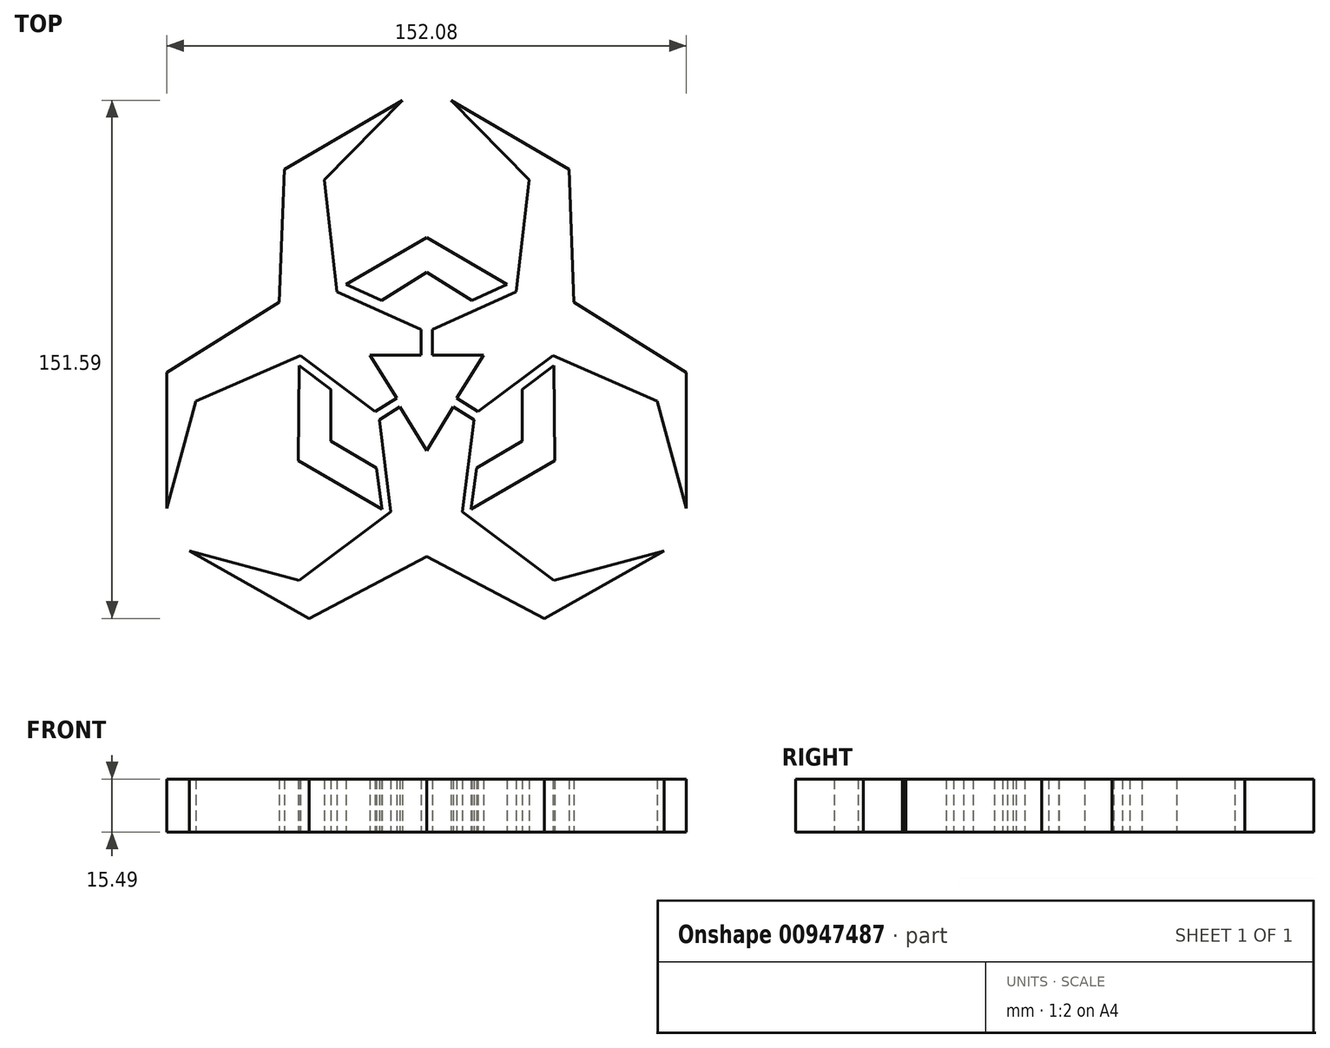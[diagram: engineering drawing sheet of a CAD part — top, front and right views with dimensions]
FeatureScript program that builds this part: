
annotation { "Feature Type Name" : "Feature", "Feature Type Description" : "" }
export const myFeature = defineFeature(function(context is Context, id is Id, definition is map)
    precondition{}
    {
        {
            var Q0;
            Q0=qCreatedBy(makeId("Top.planeOp"),FACE);
            var sketch = newSketch(context, id + "F0", { "sketchPlane" : qUnion([Q0])});
            skLineSegment(sketch, "E0", {"start": v(-13.19, 17.58) * mm, "end": v(-23.54, 22.27) * mm});
            skLineSegment(sketch, "E1", {"start": v(-23.54, 22.27) * mm, "end": v(0, 35.95) * mm});
            skLineSegment(sketch, "E2", {"start": v(0, 35.95) * mm, "end": v(0, 25.8) * mm});
            skLineSegment(sketch, "E3", {"start": v(0, 25.8) * mm, "end": v(-13.19, 17.58) * mm});
            skLineSegment(sketch, "E4.MirrorCS", {"start": v(23.54, 22.27) * mm, "end": v(0, 35.95) * mm});
            skLineSegment(sketch, "E5.MirrorCS", {"start": v(0, 25.8) * mm, "end": v(13.19, 17.58) * mm});
            skLineSegment(sketch, "E6.MirrorCS", {"start": v(13.19, 17.58) * mm, "end": v(23.54, 22.27) * mm});
            skLineSegment(sketch, "E7", {"start": v(-7.1, 76.07) * mm, "end": v(-41.67, 55.83) * mm});
            skLineSegment(sketch, "E8", {"start": v(-41.67, 55.83) * mm, "end": v(-43.14, 17.08) * mm});
            skLineSegment(sketch, "E9", {"start": v(-43.14, 17.08) * mm, "end": v(-76.04, -3.52) * mm});
            skLineSegment(sketch, "E10", {"start": v(-76.04, -3.52) * mm, "end": v(-76, -43.3) * mm});
            skLineSegment(sketch, "E11", {"start": v(-76, -43.3) * mm, "end": v(-67.53, -11.95) * mm});
            skLineSegment(sketch, "E12", {"start": v(-67.53, -11.95) * mm, "end": v(-36.97, 1.41) * mm});
            skLineSegment(sketch, "E13", {"start": v(-36.97, 1.41) * mm, "end": v(-15.01, -14.97) * mm});
            skLineSegment(sketch, "E14", {"start": v(-15.01, -14.97) * mm, "end": v(-8.76, -11.05) * mm});
            skLineSegment(sketch, "E15", {"start": v(-8.76, -11.05) * mm, "end": v(-16.63, 1.52) * mm});
            skLineSegment(sketch, "E16", {"start": v(-16.63, 1.52) * mm, "end": v(-1.65, 1.53) * mm});
            skLineSegment(sketch, "E17", {"start": v(-1.65, 1.53) * mm, "end": v(-1.66, 9.08) * mm});
            skLineSegment(sketch, "E18", {"start": v(-1.66, 9.08) * mm, "end": v(-26.24, 20.12) * mm});
            skLineSegment(sketch, "E19", {"start": v(-26.24, 20.12) * mm, "end": v(-29.96, 52.9) * mm});
            skLineSegment(sketch, "E20", {"start": v(-29.96, 52.9) * mm, "end": v(-7.1, 76.07) * mm});
            skLineSegment(sketch, "E21", {"start": v(-37.27, -1.5) * mm, "end": v(-28, -8.54) * mm});
            skLineSegment(sketch, "E22", {"start": v(-28, -8.54) * mm, "end": v(-28, -23.58) * mm});
            skLineSegment(sketch, "E23", {"start": v(-28, -23.58) * mm, "end": v(-14.7, -31.5) * mm});
            skLineSegment(sketch, "E24", {"start": v(-14.7, -31.5) * mm, "end": v(-13.03, -43.5) * mm});
            skLineSegment(sketch, "E25", {"start": v(-13.03, -43.5) * mm, "end": v(-37.54, -29.34) * mm});
            skLineSegment(sketch, "E26", {"start": v(-37.54, -29.34) * mm, "end": v(-37.27, -1.5) * mm});
            skLineSegment(sketch, "E27", {"start": v(0, -26.47) * mm, "end": v(0, -57.34) * mm});
            skLineSegment(sketch, "E28", {"start": v(0, -57.34) * mm, "end": v(-34.42, -75.52) * mm});
            skLineSegment(sketch, "E29", {"start": v(-34.42, -75.52) * mm, "end": v(-69.48, -55.78) * mm});
            skLineSegment(sketch, "E30", {"start": v(-69.48, -55.78) * mm, "end": v(-37.27, -64.33) * mm});
            skLineSegment(sketch, "E31", {"start": v(-37.27, -64.33) * mm, "end": v(-10.5, -44.28) * mm});
            skLineSegment(sketch, "E32", {"start": v(-10.5, -44.28) * mm, "end": v(-13.84, -17.43) * mm});
            skLineSegment(sketch, "E33", {"start": v(-13.84, -17.43) * mm, "end": v(-7.8, -13.6) * mm});
            skLineSegment(sketch, "E34", {"start": v(-7.8, -13.6) * mm, "end": v(0, -26.47) * mm});
            skLineSegment(sketch, "E35.MirrorCS", {"start": v(29.96, 52.9) * mm, "end": v(7.1, 76.07) * mm});
            skLineSegment(sketch, "E36.MirrorCS", {"start": v(7.1, 76.07) * mm, "end": v(41.67, 55.83) * mm});
            skLineSegment(sketch, "E37.MirrorCS", {"start": v(41.67, 55.83) * mm, "end": v(43.14, 17.08) * mm});
            skLineSegment(sketch, "E38.MirrorCS", {"start": v(26.24, 20.12) * mm, "end": v(29.96, 52.9) * mm});
            skLineSegment(sketch, "E39.MirrorCS", {"start": v(1.66, 9.08) * mm, "end": v(26.24, 20.12) * mm});
            skLineSegment(sketch, "E40.MirrorCS", {"start": v(16.63, 1.52) * mm, "end": v(1.65, 1.53) * mm});
            skLineSegment(sketch, "E41.MirrorCS", {"start": v(1.65, 1.53) * mm, "end": v(1.66, 9.08) * mm});
            skLineSegment(sketch, "E42.MirrorCS", {"start": v(13.84, -17.43) * mm, "end": v(7.8, -13.6) * mm});
            skLineSegment(sketch, "E43.MirrorCS", {"start": v(7.8, -13.6) * mm, "end": v(0, -26.47) * mm});
            skLineSegment(sketch, "E44.MirrorCS", {"start": v(8.76, -11.05) * mm, "end": v(16.63, 1.52) * mm});
            skLineSegment(sketch, "E45.MirrorCS", {"start": v(15.01, -14.97) * mm, "end": v(8.76, -11.05) * mm});
            skLineSegment(sketch, "E46.MirrorCS", {"start": v(36.97, 1.41) * mm, "end": v(15.01, -14.97) * mm});
            skLineSegment(sketch, "E47.MirrorCS", {"start": v(28, -8.54) * mm, "end": v(28, -23.58) * mm});
            skLineSegment(sketch, "E48.MirrorCS", {"start": v(37.27, -1.5) * mm, "end": v(28, -8.54) * mm});
            skLineSegment(sketch, "E49.MirrorCS", {"start": v(37.54, -29.34) * mm, "end": v(37.27, -1.5) * mm});
            skLineSegment(sketch, "E50.MirrorCS", {"start": v(13.03, -43.5) * mm, "end": v(37.54, -29.34) * mm});
            skLineSegment(sketch, "E51.MirrorCS", {"start": v(28, -23.58) * mm, "end": v(14.7, -31.5) * mm});
            skLineSegment(sketch, "E52.MirrorCS", {"start": v(14.7, -31.5) * mm, "end": v(13.03, -43.5) * mm});
            skLineSegment(sketch, "E53.MirrorCS", {"start": v(37.27, -64.33) * mm, "end": v(10.5, -44.28) * mm});
            skLineSegment(sketch, "E54.MirrorCS", {"start": v(10.5, -44.28) * mm, "end": v(13.84, -17.43) * mm});
            skLineSegment(sketch, "E55.MirrorCS", {"start": v(0, -57.34) * mm, "end": v(34.42, -75.52) * mm});
            skLineSegment(sketch, "E56.MirrorCS", {"start": v(34.42, -75.52) * mm, "end": v(69.48, -55.78) * mm});
            skLineSegment(sketch, "E57.MirrorCS", {"start": v(69.48, -55.78) * mm, "end": v(37.27, -64.33) * mm});
            skLineSegment(sketch, "E58.MirrorCS", {"start": v(67.53, -11.95) * mm, "end": v(36.97, 1.41) * mm});
            skLineSegment(sketch, "E59.MirrorCS", {"start": v(76, -43.3) * mm, "end": v(67.53, -11.95) * mm});
            skLineSegment(sketch, "E60.MirrorCS", {"start": v(76.04, -3.52) * mm, "end": v(76, -43.3) * mm});
            skLineSegment(sketch, "E61.MirrorCS", {"start": v(43.14, 17.08) * mm, "end": v(76.04, -3.52) * mm});
            skSolve(sketch);
        }
        {
            var Q0;
            Q0=makeQuery(id+"F0.imprint","IMPRINT",FACE,{"disambiguationData":[TD([[makeQuery(id+"F0.imprint","IMPRINT",EDGE,{"derivedFrom":sQuery(id+"F0.wireOp",EDGE,"E7")}),1.0]])]});
            var Q1;
            Q1=makeQuery(id+"F0.imprint","IMPRINT",FACE,{"disambiguationData":[TD([[makeQuery(id+"F0.imprint","IMPRINT",EDGE,{"derivedFrom":sQuery(id+"F0.wireOp",EDGE,"E35.MirrorCS")}),-1.0]])]});
            var Q2;
            Q2=makeQuery(id+"F0.imprint","IMPRINT",FACE,{"disambiguationData":[TD([[makeQuery(id+"F0.imprint","IMPRINT",EDGE,{"derivedFrom":sQuery(id+"F0.wireOp",EDGE,"E0")}),-1.0]])]});
            var Q3;
            Q3=makeQuery(id+"F0.imprint","IMPRINT",FACE,{"disambiguationData":[TD([[makeQuery(id+"F0.imprint","IMPRINT",EDGE,{"derivedFrom":sQuery(id+"F0.wireOp",EDGE,"E2")}),1.0]])]});
            var Q4;
            Q4=makeQuery(id+"F0.imprint","IMPRINT",FACE,{"disambiguationData":[TD([[makeQuery(id+"F0.imprint","IMPRINT",EDGE,{"derivedFrom":sQuery(id+"F0.wireOp",EDGE,"E27")}),-1.0]])]});
            var Q5;
            Q5=makeQuery(id+"F0.imprint","IMPRINT",FACE,{"disambiguationData":[TD([[makeQuery(id+"F0.imprint","IMPRINT",EDGE,{"derivedFrom":sQuery(id+"F0.wireOp",EDGE,"E27")}),1.0]])]});
            var Q6;
            Q6=makeQuery(id+"F0.imprint","IMPRINT",FACE,{"disambiguationData":[TD([[makeQuery(id+"F0.imprint","IMPRINT",EDGE,{"derivedFrom":sQuery(id+"F0.wireOp",EDGE,"E21")}),-1.0]])]});
            var Q7;
            Q7=makeQuery(id+"F0.imprint","IMPRINT",FACE,{"disambiguationData":[TD([[makeQuery(id+"F0.imprint","IMPRINT",EDGE,{"derivedFrom":sQuery(id+"F0.wireOp",EDGE,"E47.MirrorCS")}),1.0]])]});
            extrude(context, id + "F1", {"entities" : qUnion([Q0, Q1, Q2, Q3, Q4, Q5, Q6, Q7]), "depth" : 15.5 * mm, "offsetDistance" : 25.4 * mm});
        }
    });
